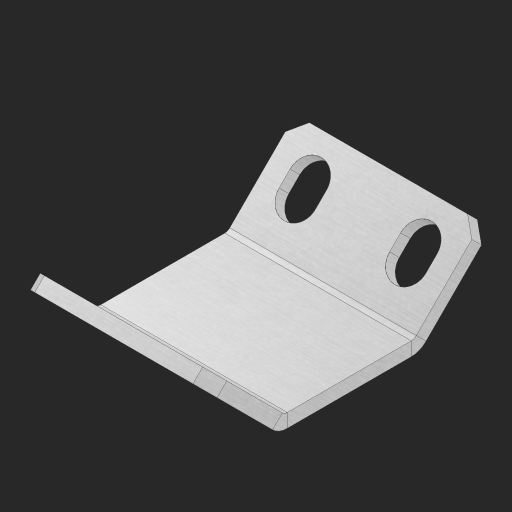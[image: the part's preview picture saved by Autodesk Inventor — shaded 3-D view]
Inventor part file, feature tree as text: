
AUTODESK INVENTOR PART (.ipt)
format: ipt  version: 2023 (Build 270158000, 158)  size: 238,592 bytes
history: native  units: in
note: dims shown in document units (in); Inventor stores cm internally (conversion verified against a paired STEP export)
features: chamfer x1, other x1, imported_body x1
ambient origin geometry x8: Origin, YZ Plane, XZ Plane, XY Plane, X Axis, Y Axis, Z Axis, Center Point
bodies: Body1 (feature_tree)
feature tree (3):
  chamfer  "Chamfer1"  [1 undecoded]
  other  "90-Degree Gusset Angle"
  imported_body  "Base1"
note: 1 required parameter value undecoded (feature->parameter linkage not recoverable at this tier; creation-order binding heuristic only, values carry confidence <= 0.55)
